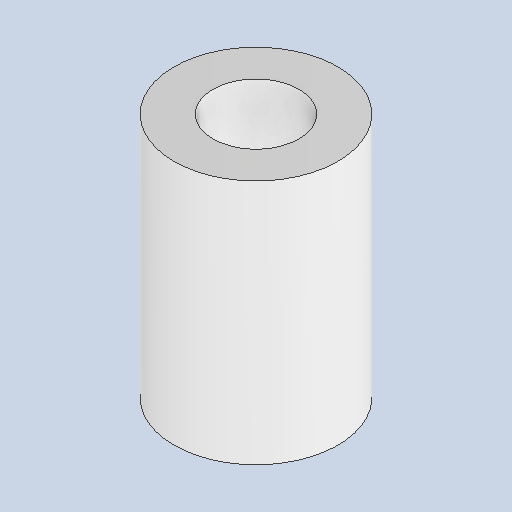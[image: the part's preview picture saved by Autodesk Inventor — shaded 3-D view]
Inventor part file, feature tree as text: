
AUTODESK INVENTOR PART (.ipt)
format: ipt  version: 2024.2 (Build 282272000, 272)  size: 97,280 bytes
history: native  units: mm
features: revolve x1, sketch x1
ambient origin geometry x8: Origin, YZ Plane, XZ Plane, XY Plane, X Axis, Y Axis, Z Axis, Center Point
bodies: Solid1 (feature_tree)
feature tree (2):
  revolve  "Revolution1"  [1 undecoded]
  sketch  "Sketch1"  dims[d0=6.0mm d1=2.1mm d2=4.0mm d3=90.0deg]
note: 1 required parameter value undecoded (feature->parameter linkage not recoverable at this tier; creation-order binding heuristic only, values carry confidence <= 0.55)
